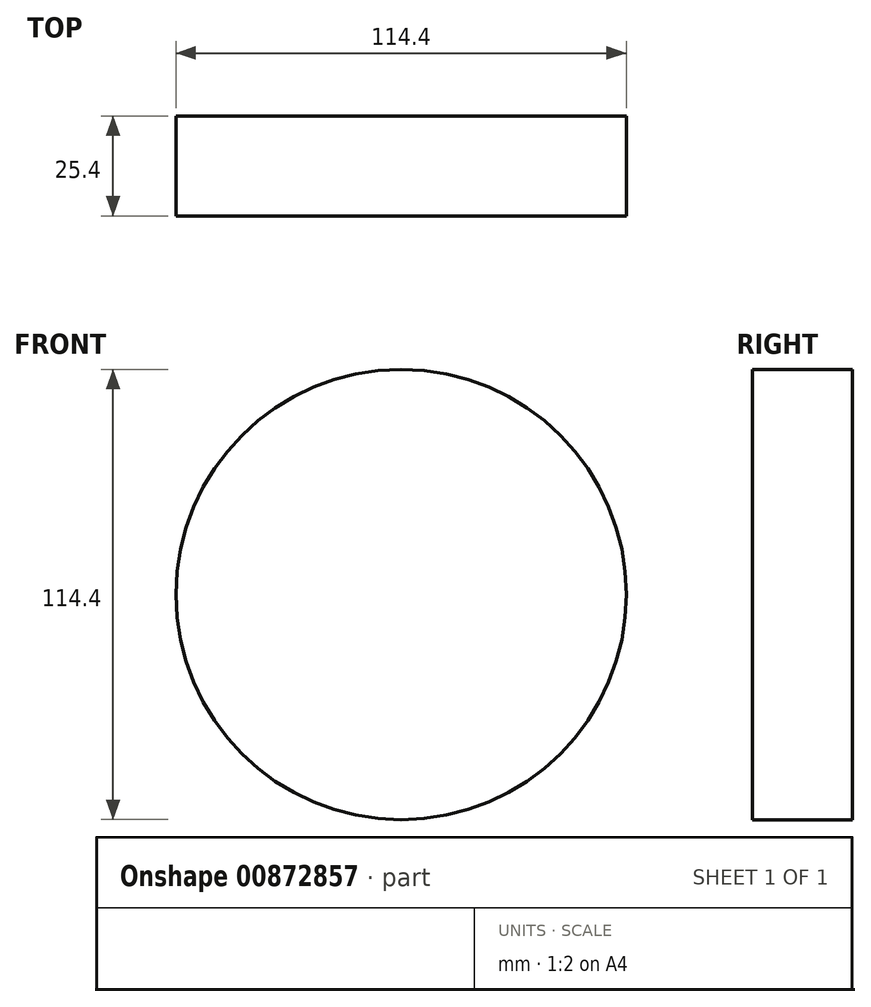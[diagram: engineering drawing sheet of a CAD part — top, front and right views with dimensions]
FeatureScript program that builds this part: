
annotation { "Feature Type Name" : "Feature", "Feature Type Description" : "" }
export const myFeature = defineFeature(function(context is Context, id is Id, definition is map)
    precondition{}
    {
        {
            var Q0;
            Q0=qCreatedBy(makeId("Front.planeOp"),FACE);
            var sketch = newSketch(context, id + "F0", { "sketchPlane" : qUnion([Q0])});
            skCircle(sketch, "E0", {"center": v(0, 0) * mm, "radius": 57.2 * mm});
            skSolve(sketch);
        }
        {
            var Q0;
            Q0=qSketchRegion(id+"F0",true);
            extrude(context, id + "F1", {"entities" : qUnion([Q0]), "depth" : 25.4 * mm, "offsetDistance" : 25.4 * mm});
        }
    });
